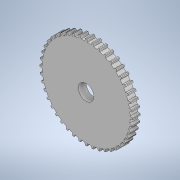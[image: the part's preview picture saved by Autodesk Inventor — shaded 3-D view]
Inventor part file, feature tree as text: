
AUTODESK INVENTOR PART (.ipt)
format: ipt  version: 2021 (Build 250183000, 183)  size: 408,064 bytes
history: native  units: in
note: dims shown in document units (in); Inventor stores cm internally (conversion verified against a paired STEP export)
features: extrude x1, sketch x1
ambient origin geometry x8: Origin, YZ Plane, XZ Plane, XY Plane, X Axis, Y Axis, Z Axis, Center Point
bodies: Solid1 (feature_tree)
feature tree (2):
  extrude  "Extrusion1"  [1 undecoded]
  sketch  "Sketch1"  dims[d0=0.7874in d1=0.0in]
note: 1 required parameter value undecoded (feature->parameter linkage not recoverable at this tier; creation-order binding heuristic only, values carry confidence <= 0.55)
